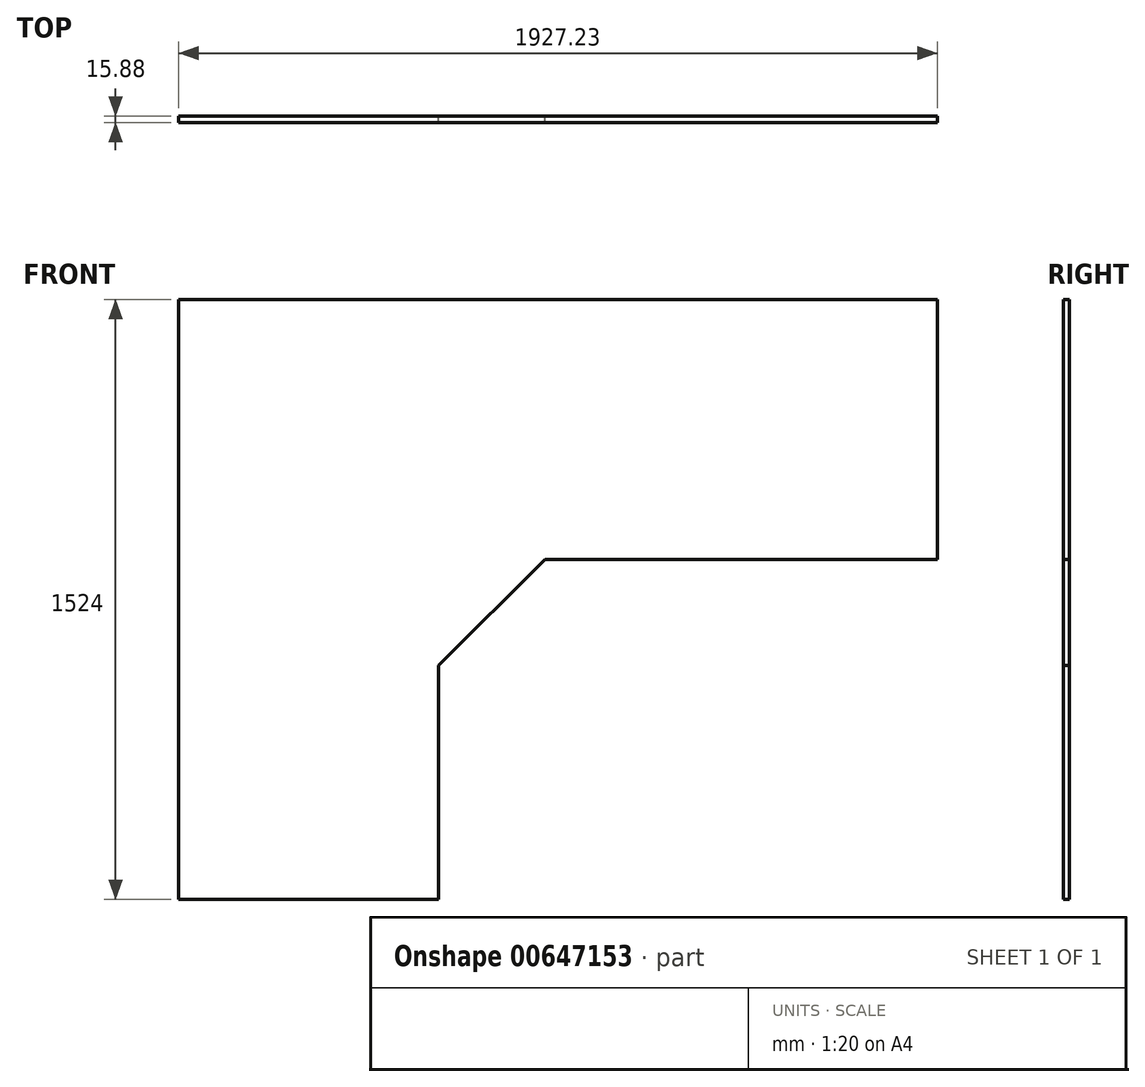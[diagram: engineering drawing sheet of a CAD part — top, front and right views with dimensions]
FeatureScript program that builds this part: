
annotation { "Feature Type Name" : "Feature", "Feature Type Description" : "" }
export const myFeature = defineFeature(function(context is Context, id is Id, definition is map)
    precondition{}
    {
        {
            var Q0;
            Q0=qCreatedBy(makeId("Front.planeOp"),FACE);
            var sketch = newSketch(context, id + "F0", { "sketchPlane" : qUnion([Q0])});
            skLineSegment(sketch, "E0", {"start": v(-68.34, 741.29) * mm, "end": v(1858.89, 741.29) * mm});
            skLineSegment(sketch, "E1", {"start": v(1858.89, 741.29) * mm, "end": v(1858.89, 80.89) * mm});
            skLineSegment(sketch, "E2", {"start": v(1858.89, 80.89) * mm, "end": v(861.94, 80.89) * mm});
            skLineSegment(sketch, "E3", {"start": v(-68.34, 741.29) * mm, "end": v(-68.34, -782.71) * mm});
            skLineSegment(sketch, "E4", {"start": v(-68.34, -782.71) * mm, "end": v(592.06, -782.71) * mm});
            skLineSegment(sketch, "E5", {"start": v(592.06, -782.71) * mm, "end": v(592.06, -188.99) * mm});
            skLineSegment(sketch, "E6", {"start": v(592.06, -188.99) * mm, "end": v(861.94, 80.89) * mm});
            skSolve(sketch);
        }
        {
            var Q0;
            Q0 = qSketchRegion(id + "F0", true);
            extrude(context, id + "F1", {"entities" : qUnion([Q0]), "depth" : 15.88 * mm, "offsetDistance" : 25.4 * mm});
        }
    });
